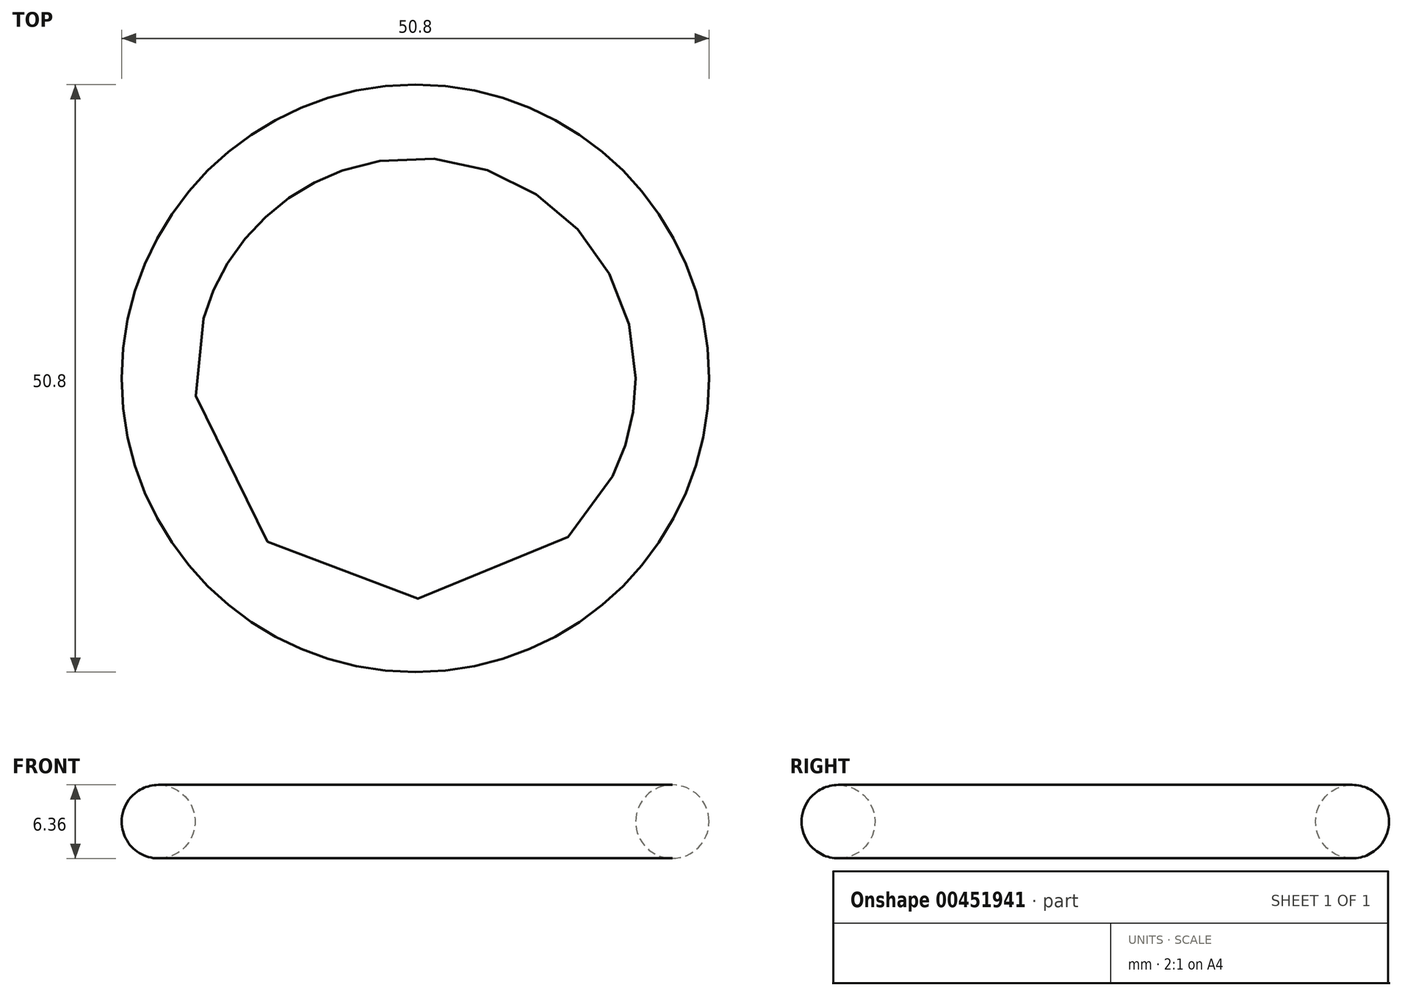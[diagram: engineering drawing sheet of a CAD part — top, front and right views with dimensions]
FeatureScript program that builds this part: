
annotation { "Feature Type Name" : "Feature", "Feature Type Description" : "" }
export const myFeature = defineFeature(function(context is Context, id is Id, definition is map)
    precondition{}
    {
        {
            var Q0;
            Q0=qCreatedBy(makeId("Front.planeOp"),FACE);
            var sketch = newSketch(context, id + "F0", { "sketchPlane" : qUnion([Q0])});
            skCircle(sketch, "E0", {"center": v(-22.22, 0) * mm, "radius": 3.18 * mm});
            skLineSegment(sketch, "E1", {"start": v(0, 27.68) * mm, "end": v(0, -25.98) * mm, "construction": true});
            skSolve(sketch);
        }
        {
            var Q0;
            Q0 = qSketchRegion(id + "F0", true);
            var Q1;
            Q1=sQuery(id+"F0.wireOp",EDGE,"E1");
            revolve(context, id + "F1", {"entities" : qUnion([Q0]), "axis" : qUnion([Q1]), "revolveType" : RevolveType.FULL});
        }
    });
